# Revit family: XMRS1HO
name_source: partatom
category: Lighting Fixtures
units: mm (PartAtom-declared; Revit-internal decimal feet)

## family parameters
Cut with Voids When Loaded = No
Host = Face
Light Source = Yes
Maintain Annotation Orientation = No
Part Type = Normal
Room Calculation Point = No
Round Connector Dimension = Use Diameter
Shared = No

## types (1)
- XMRS1HO
    Color Filter = 16777215
    Default Elevation = 1219 mm
    Dimming Lamp Color Temperature Shift = <None>
    Emit from Line Length = 610 mm
    HOUSING MATERIAL = HOUSING MATERIAL
    LED BOARD MATERIAL = LED BOARD MATERIAL
    LED MATERIAL = LED MATERIAL
    LENS MATERIAL = LENS MATERIAL
    Lamp = LED
    Manufacturer = BEGHELLI
    Model = XMRS1LED7W
    Photometric Web File = XMRS1-LED-7W.ies
    Tilt Angle = 0.00°
    Type Comments = The XMR is configured with a 120/277VAC input. Standard features 
include solid-state charging circuitry, low voltage disconnect, AC 
lockout and brownout protection. Maintenance free 6V 4.5Ah sealed 
lead calcium battery.
    Type Image = XMR IMAGE.png
    Wattage Comments = 7

## geometry (parser evidence)
native form markers: Sweep x9
no freeform markers — native parametric forms only
